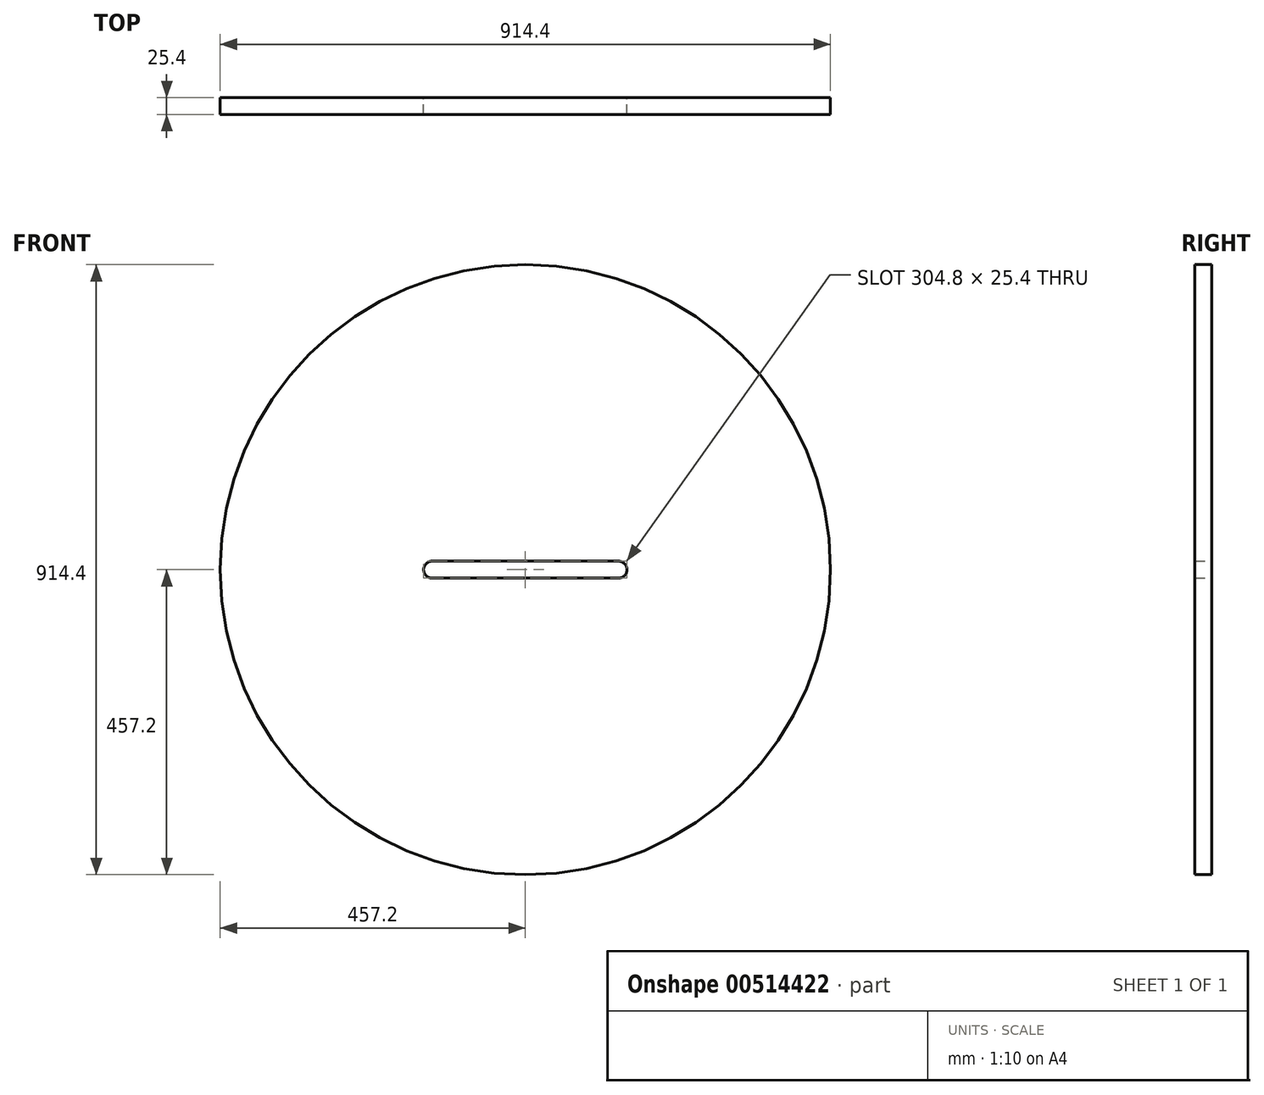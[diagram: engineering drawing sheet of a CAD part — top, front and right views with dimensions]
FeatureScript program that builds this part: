
annotation { "Feature Type Name" : "Feature", "Feature Type Description" : "" }
export const myFeature = defineFeature(function(context is Context, id is Id, definition is map)
    precondition{}
    {
        {
            var Q0;
            Q0=qCreatedBy(makeId("Front.planeOp"),FACE);
            var sketch = newSketch(context, id + "F0", { "sketchPlane" : qUnion([Q0])});
            skLineSegment(sketch, "E0.bottom", {"start": v(-139.7, 12.7) * mm, "end": v(139.7, 12.7) * mm});
            skLineSegment(sketch, "E0.top", {"start": v(-139.7, -12.7) * mm, "end": v(139.7, -12.7) * mm});
            skLineSegment(sketch, "E0.left", {"start": v(-139.7, 12.7) * mm, "end": v(-139.7, -12.7) * mm});
            skLineSegment(sketch, "E0.right", {"start": v(139.7, 12.7) * mm, "end": v(139.7, -12.7) * mm});
            skArc(sketch, "E1", {"start": v(-139.7, 12.7) * mm, "mid": v(-152.4, 0) * mm, "end": v(-139.7, -12.7) * mm});
            skArc(sketch, "E2", {"start": v(139.7, -12.7) * mm, "mid": v(152.4, 0) * mm, "end": v(139.7, 12.7) * mm});
            skCircle(sketch, "E3", {"center": v(0, 0) * mm, "radius": 457.2 * mm});
            skSolve(sketch);
        }
        {
            var Q0;
            Q0=makeQuery(id+"F0.imprint","IMPRINT",FACE,{"disambiguationData":[TD([[makeQuery(id+"F0.imprint","IMPRINT",EDGE,{"derivedFrom":sQuery(id+"F0.wireOp",EDGE,"E0.bottom")}),1.0]])]});
            extrude(context, id + "F1", {"entities" : qUnion([Q0]), "depth" : 25.4 * mm, "offsetDistance" : 25.4 * mm});
        }
    });
